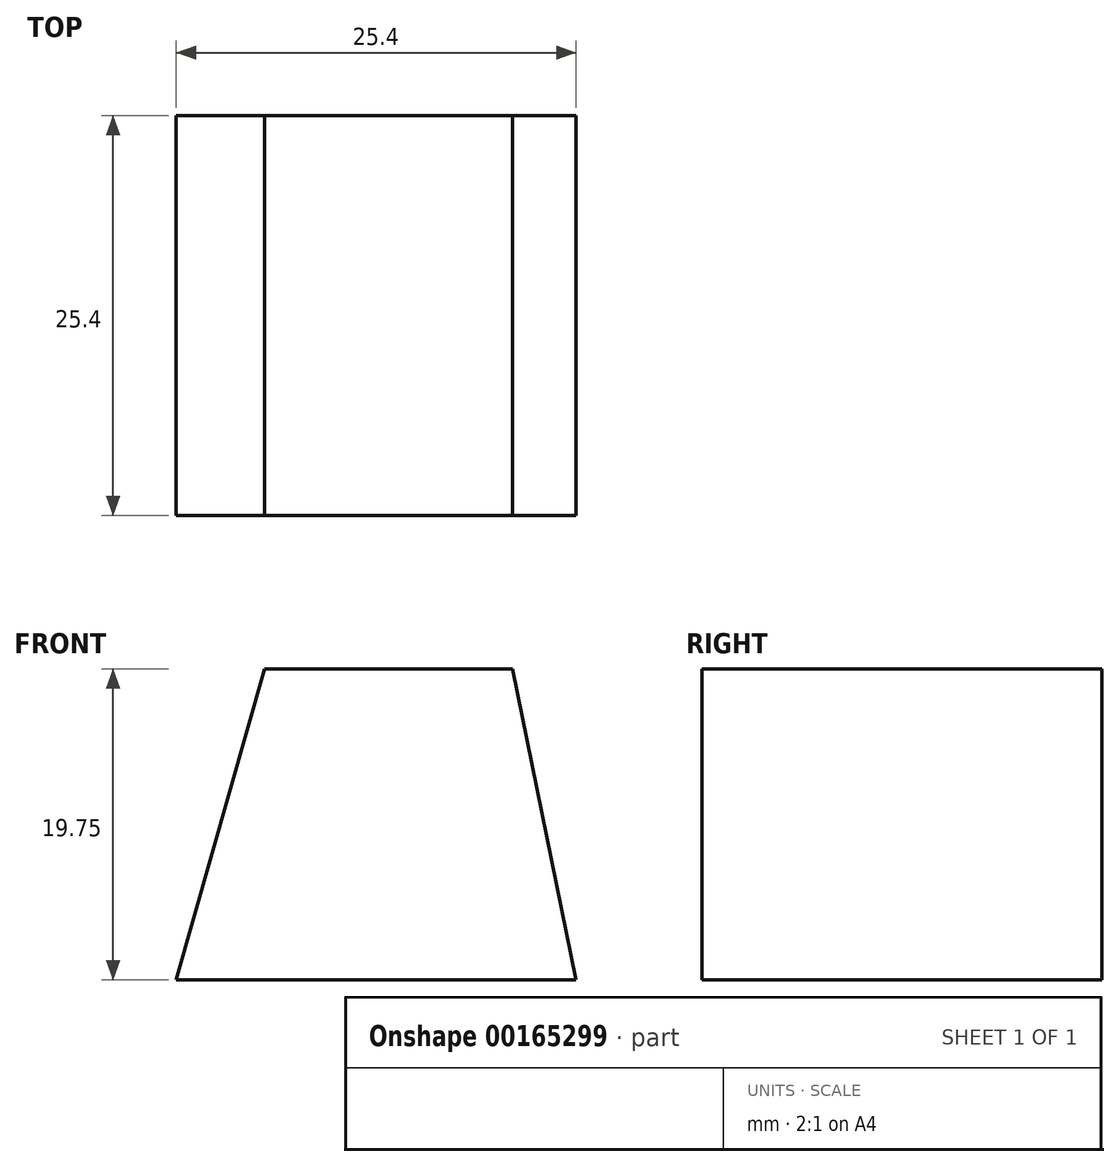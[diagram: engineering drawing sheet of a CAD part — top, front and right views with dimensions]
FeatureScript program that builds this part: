
annotation { "Feature Type Name" : "Feature", "Feature Type Description" : "" }
export const myFeature = defineFeature(function(context is Context, id is Id, definition is map)
    precondition{}
    {
        {
            var Q0;
            Q0=qCreatedBy(makeId("Front.planeOp"),FACE);
            var sketch = newSketch(context, id + "F0", { "sketchPlane" : qUnion([Q0])});
            skLineSegment(sketch, "E0", {"start": v(-16.35, 0) * mm, "end": v(9.05, 0) * mm});
            skLineSegment(sketch, "E1", {"start": v(-16.35, 0) * mm, "end": v(-10.75, 19.75) * mm});
            skLineSegment(sketch, "E2", {"start": v(-10.75, 19.75) * mm, "end": v(5, 19.75) * mm});
            skLineSegment(sketch, "E3", {"start": v(5, 19.75) * mm, "end": v(9.05, 0) * mm});
            skSolve(sketch);
        }
        {
            var Q0;
            Q0=makeQuery(id+"F0.imprint","IMPRINT",FACE,{"disambiguationData":[TD([[makeQuery(id+"F0.imprint","IMPRINT",EDGE,{"derivedFrom":sQuery(id+"F0.wireOp",EDGE,"E0")}),1.0]])]});
            extrude(context, id + "F1", {"entities" : qUnion([Q0]), "depth" : 25.4 * mm});
        }
    });
